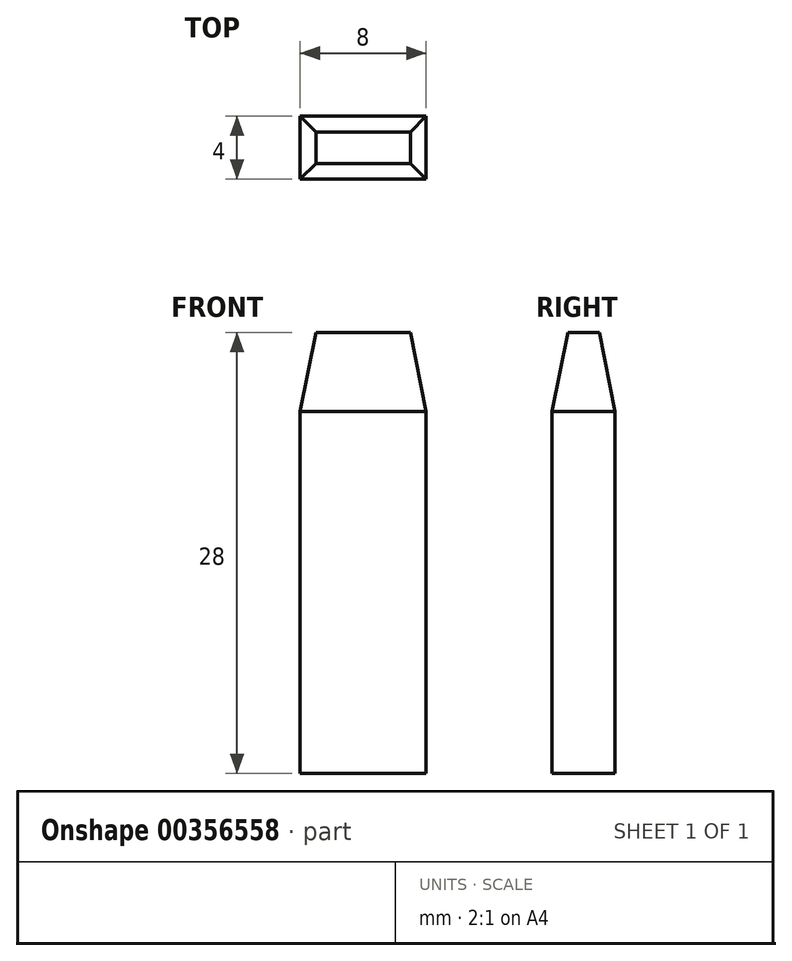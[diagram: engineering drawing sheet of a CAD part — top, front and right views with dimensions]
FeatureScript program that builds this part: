
annotation { "Feature Type Name" : "Feature", "Feature Type Description" : "" }
export const myFeature = defineFeature(function(context is Context, id is Id, definition is map)
    precondition{}
    {
        {
            var Q0;
            Q0=qCreatedBy(makeId("Top.planeOp"),FACE);
            var sketch = newSketch(context, id + "F0", { "sketchPlane" : qUnion([Q0])});
            skLineSegment(sketch, "E0.bottom", {"start": v(-15.08, 0) * mm, "end": v(-7.08, 0) * mm});
            skLineSegment(sketch, "E0.top", {"start": v(-15.08, -4) * mm, "end": v(-7.08, -4) * mm});
            skLineSegment(sketch, "E0.left", {"start": v(-15.08, 0) * mm, "end": v(-15.08, -4) * mm});
            skLineSegment(sketch, "E0.right", {"start": v(-7.08, 0) * mm, "end": v(-7.08, -4) * mm});
            skSolve(sketch);
        }
        {
            var Q0;
            Q0=makeQuery(id+"F0.imprint","IMPRINT",FACE,{"disambiguationData":[TD([[makeQuery(id+"F0.imprint","IMPRINT",EDGE,{"derivedFrom":sQuery(id+"F0.wireOp",EDGE,"E0.bottom")}),-1.0]])]});
            extrude(context, id + "F1", {"entities" : qUnion([Q0]), "depth" : 28 * mm});
        }
        {
            var Q0;
            Q0=makeQuery(id+"F1.opExtrude","CAP_EDGE",EDGE,{"disambiguationData":[OSD([sQuery(id+"F0.wireOp",EDGE,"E0.bottom")])],"isStart":false});
            var Q1;
            Q1=makeQuery(id+"F1.opExtrude","CAP_EDGE",EDGE,{"disambiguationData":[OSD([sQuery(id+"F0.wireOp",EDGE,"E0.top")])],"isStart":false});
            var Q2;
            Q2=makeQuery(id+"F1.opExtrude","CAP_EDGE",EDGE,{"disambiguationData":[OSD([sQuery(id+"F0.wireOp",EDGE,"E0.right")])],"isStart":false});
            var Q3;
            Q3=makeQuery(id+"F1.opExtrude","CAP_EDGE",EDGE,{"disambiguationData":[OSD([sQuery(id+"F0.wireOp",EDGE,"E0.left")])],"isStart":false});
            chamfer(context, id + "F2", {"entities" : qUnion([Q0, Q1, Q2, Q3]), "chamferType" : ChamferType.TWO_OFFSETS, "width1" : 5 * mm, "oppositeDirection" : false, "width2" : 1 * mm, "tangentPropagation" : true});
        }
    });
